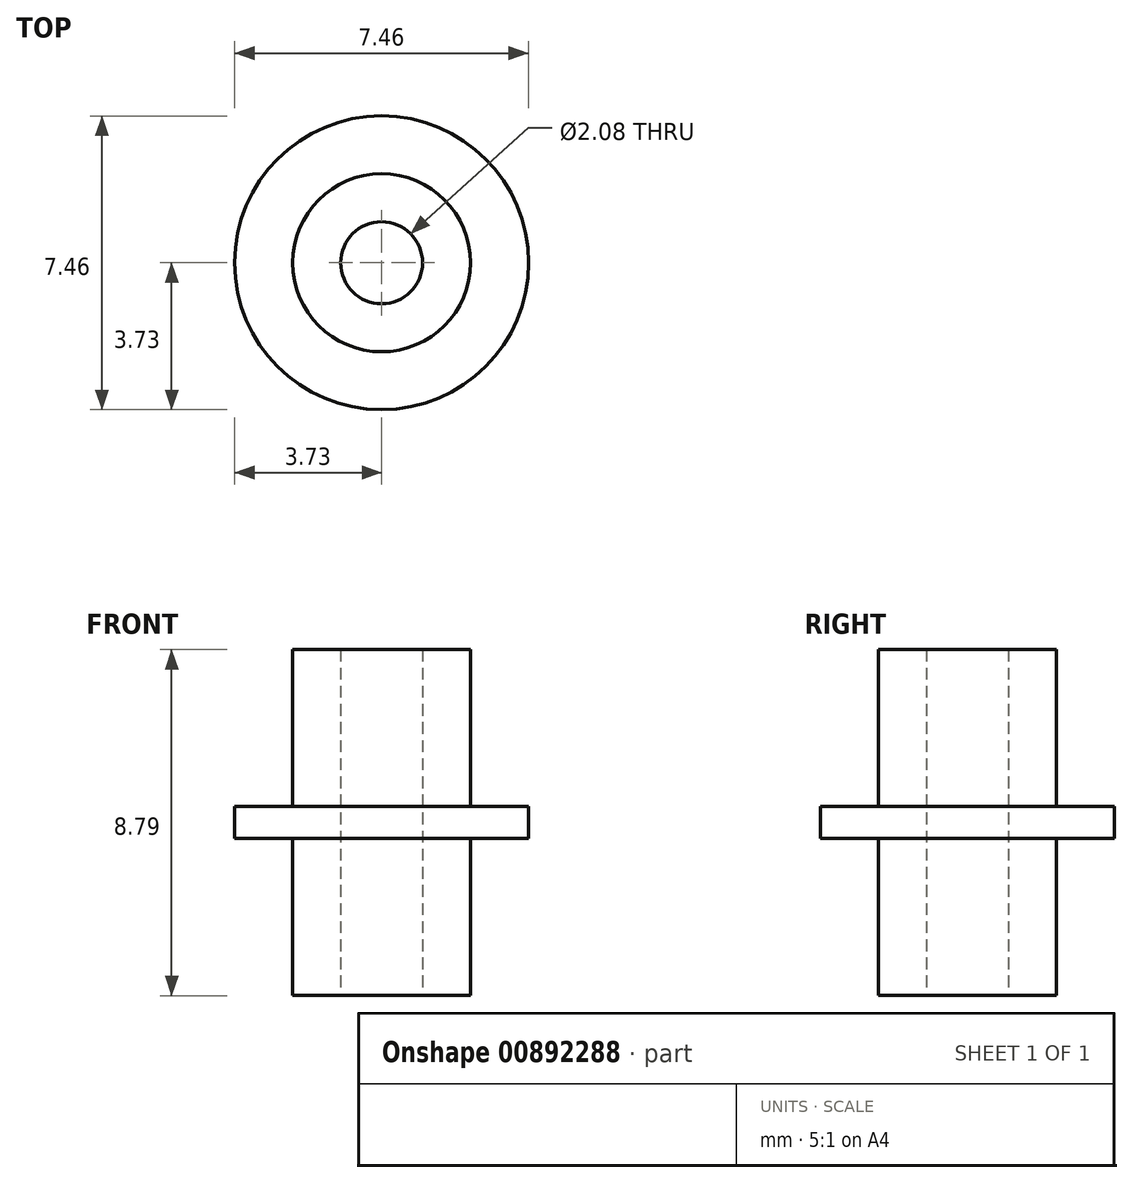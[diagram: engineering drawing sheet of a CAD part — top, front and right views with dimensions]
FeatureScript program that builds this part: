
annotation { "Feature Type Name" : "Feature", "Feature Type Description" : "" }
export const myFeature = defineFeature(function(context is Context, id is Id, definition is map)
    precondition{}
    {
        {
            var Q0;
            Q0=qCreatedBy(makeId("Top.planeOp"),FACE);
            var sketch = newSketch(context, id + "F0", { "sketchPlane" : qUnion([Q0])});
            skCircle(sketch, "E0", {"center": v(0, 0) * mm, "radius": 3.73 * mm});
            skSolve(sketch);
        }
        {
            var Q0;
            Q0 = qSketchRegion(id + "F0", true);
            extrude(context, id + "F1", {"entities" : qUnion([Q0]), "depth" : 0.81 * mm, "offsetDistance" : 25.4 * mm});
        }
        {
            var Q0;
            Q0=makeQuery(id+"F1.opExtrude","CAP_FACE",FACE,{"disambiguationData":[OSD([sQuery(id+"F0.wireOp",EDGE,"E0")])],"isStart":true});
            var sketch = newSketch(context, id + "F2", { "sketchPlane" : qUnion([Q0])});
            skCircle(sketch, "E1", {"center": v(0, 0) * mm, "radius": 2.26 * mm});
            skSolve(sketch);
        }
        {
            var Q0;
            Q0=makeQuery(id+"F2.imprint","IMPRINT",FACE,{"disambiguationData":[TD([[makeQuery(id+"F2.imprint","IMPRINT",EDGE,{"derivedFrom":sQuery(id+"F2.wireOp",EDGE,"E1")}),1.0]])]});
            extrude(context, id + "F3", {"entities" : qUnion([Q0]), "operationType" : NewBodyOperationType.ADD, "depth" : 4 * mm, "offsetDistance" : 25.4 * mm});
        }
        {
            var Q0;
            Q0=makeQuery(id+"F1.opExtrude","CAP_FACE",FACE,{"disambiguationData":[OSD([sQuery(id+"F0.wireOp",EDGE,"E0")])],"isStart":false});
            var sketch = newSketch(context, id + "F4", { "sketchPlane" : qUnion([Q0])});
            skCircle(sketch, "E2.0", {"center": v(0, 0) * mm, "radius": 2.26 * mm});
            skSolve(sketch);
        }
        {
            var Q0;
            Q0 = qSketchRegion(id + "F4", true);
            extrude(context, id + "F5", {"entities" : qUnion([Q0]), "operationType" : NewBodyOperationType.ADD, "depth" : 4 * mm, "offsetDistance" : 25.4 * mm});
        }
        {
            var Q0;
            Q0=makeQuery(id+"F3.opExtrude","CAP_FACE",FACE,{"disambiguationData":[OSD([sQuery(id+"F2.wireOp",EDGE,"E1")])],"isStart":false});
            var sketch = newSketch(context, id + "F6", { "sketchPlane" : qUnion([Q0])});
            skCircle(sketch, "E3", {"center": v(0, 0) * mm, "radius": 1.04 * mm});
            skSolve(sketch);
        }
        {
            var Q0;
            Q0=makeQuery(id+"F6.imprint","IMPRINT",FACE,{"disambiguationData":[TD([[makeQuery(id+"F6.imprint","IMPRINT",EDGE,{"derivedFrom":sQuery(id+"F6.wireOp",EDGE,"E3")}),1.0]])]});
            extrude(context, id + "F7", {"entities" : qUnion([Q0]), "operationType" : NewBodyOperationType.REMOVE, "oppositeDirection" : true, "depth" : 25.4 * mm, "offsetDistance" : 25.4 * mm});
        }
    });
